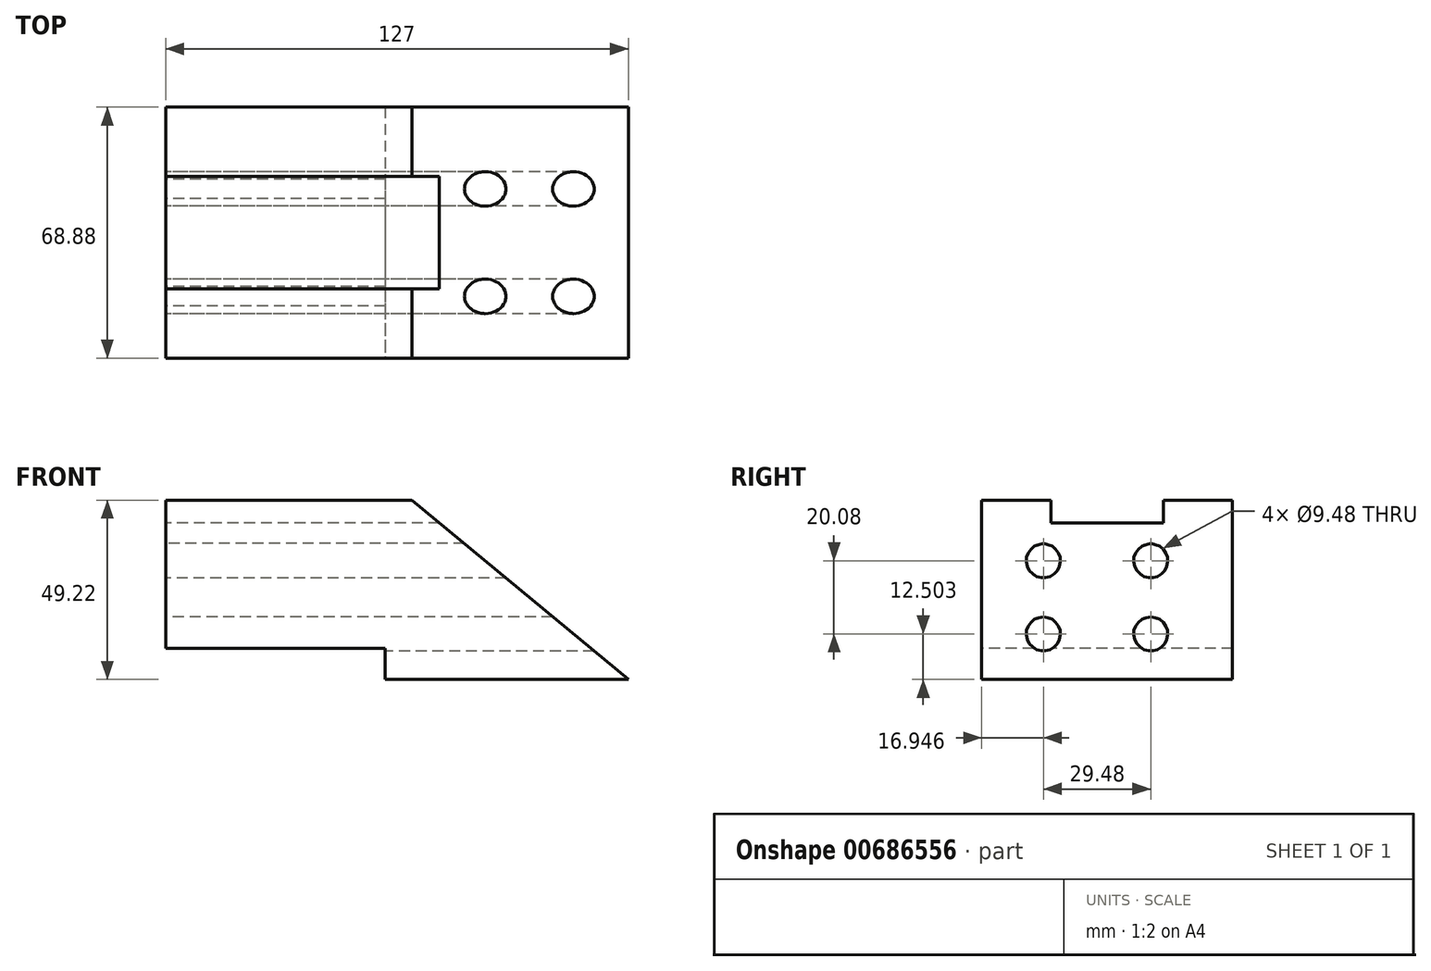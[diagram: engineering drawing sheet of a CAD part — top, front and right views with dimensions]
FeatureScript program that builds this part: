
annotation { "Feature Type Name" : "Feature", "Feature Type Description" : "" }
export const myFeature = defineFeature(function(context is Context, id is Id, definition is map)
    precondition{}
    {
        {
            var Q0;
            Q0=qCreatedBy(makeId("Right.planeOp"),FACE);
            var sketch = newSketch(context, id + "F0", { "sketchPlane" : qUnion([Q0])});
            skLineSegment(sketch, "E0", {"start": v(-40.43, 25.97) * mm, "end": v(-21.38, 25.97) * mm});
            skLineSegment(sketch, "E1", {"start": v(-21.38, 25.97) * mm, "end": v(-21.38, 19.77) * mm});
            skLineSegment(sketch, "E2", {"start": v(-21.38, 19.77) * mm, "end": v(9.4, 19.77) * mm});
            skLineSegment(sketch, "E3", {"start": v(9.4, 19.77) * mm, "end": v(9.4, 25.97) * mm});
            skLineSegment(sketch, "E4", {"start": v(9.4, 25.97) * mm, "end": v(28.45, 25.97) * mm});
            skLineSegment(sketch, "E5", {"start": v(28.45, 25.97) * mm, "end": v(28.45, -23.25) * mm});
            skLineSegment(sketch, "E6", {"start": v(28.45, -23.25) * mm, "end": v(-40.43, -23.25) * mm});
            skLineSegment(sketch, "E7", {"start": v(-40.43, -23.25) * mm, "end": v(-40.43, 25.97) * mm});
            skCircle(sketch, "E8", {"center": v(-23.48, 9.33) * mm, "radius": 4.74 * mm});
            skCircle(sketch, "E9", {"center": v(6, 9.33) * mm, "radius": 4.74 * mm});
            skCircle(sketch, "E10", {"center": v(-23.48, -10.75) * mm, "radius": 4.74 * mm});
            skCircle(sketch, "E11", {"center": v(6, -10.75) * mm, "radius": 4.74 * mm});
            skSolve(sketch);
        }
        {
            var Q0;
            Q0=makeQuery(id+"F0.imprint","IMPRINT",FACE,{"disambiguationData":[TD([[makeQuery(id+"F0.imprint","IMPRINT",EDGE,{"derivedFrom":sQuery(id+"F0.wireOp",EDGE,"E0")}),-1.0]])]});
            extrude(context, id + "F1", {"entities" : qUnion([Q0]), "depth" : 101.6 * mm, "offsetDistance" : 25.4 * mm, "hasSecondDirection" : true, "secondDirectionOppositeDirection" : true, "secondDirectionDepth" : 25.4 * mm});
        }
        {
            var Q0;
            Q0=makeQuery(id+"F1.opExtrude","SWEPT_FACE",FACE,{"disambiguationData":[OSD([sQuery(id+"F0.wireOp",EDGE,"E7")])]});
            var sketch = newSketch(context, id + "F2", { "sketchPlane" : qUnion([Q0])});
            skLineSegment(sketch, "E12", {"start": v(42.28, 25.97) * mm, "end": v(101.6, -23.25) * mm});
            skLineSegment(sketch, "E13", {"start": v(101.6, -23.25) * mm, "end": v(101.6, 25.97) * mm});
            skLineSegment(sketch, "E14", {"start": v(101.6, 25.97) * mm, "end": v(42.28, 25.97) * mm});
            skSolve(sketch);
        }
        {
            var Q0;
            Q0=makeQuery(id+"F2.imprint","IMPRINT",FACE,{"disambiguationData":[TD([[makeQuery(id+"F2.imprint","IMPRINT",EDGE,{"derivedFrom":sQuery(id+"F2.wireOp",EDGE,"E12")}),1.0]])]});
            extrude(context, id + "F3", {"entities" : qUnion([Q0]), "operationType" : NewBodyOperationType.REMOVE, "endBound" : BoundingType.THROUGH_ALL, "oppositeDirection" : true, "depth" : 25.4 * mm, "offsetDistance" : 25.4 * mm});
        }
        {
            var Q0;
            Q0=makeQuery(id+"F1.opExtrude","SWEPT_FACE",FACE,{"disambiguationData":[OSD([sQuery(id+"F0.wireOp",EDGE,"E7")])]});
            var sketch = newSketch(context, id + "F4", { "sketchPlane" : qUnion([Q0])});
            skLineSegment(sketch, "E15", {"start": v(-25.4, -14.64) * mm, "end": v(34.9, -14.64) * mm});
            skLineSegment(sketch, "E16", {"start": v(34.9, -14.64) * mm, "end": v(34.9, -23.25) * mm});
            skLineSegment(sketch, "E17", {"start": v(34.9, -23.25) * mm, "end": v(-25.4, -23.25) * mm});
            skLineSegment(sketch, "E18", {"start": v(-25.4, -23.25) * mm, "end": v(-25.4, -14.64) * mm});
            skSolve(sketch);
        }
        {
            var Q0;
            Q0=makeQuery(id+"F4.imprint","IMPRINT",FACE,{"disambiguationData":[TD([[makeQuery(id+"F4.imprint","IMPRINT",EDGE,{"derivedFrom":sQuery(id+"F4.wireOp",EDGE,"E15")}),-1.0]])]});
            extrude(context, id + "F5", {"entities" : qUnion([Q0]), "operationType" : NewBodyOperationType.REMOVE, "endBound" : BoundingType.THROUGH_ALL, "oppositeDirection" : true, "depth" : 25.4 * mm, "offsetDistance" : 25.4 * mm});
        }
    });
